# Revit family: Door-Slider-Fleetwood-3070-XXXX
name_source: partatom
category: Doors
revit_build: Autodesk Revit 2016 (Build: 20150714_1515(x64)
units: mm (PartAtom-declared; Revit-internal decimal feet)

## family parameters
Always vertical = Yes
Cut with Voids When Loaded = No
Host = Wall
OmniClass Number = 23.30.10.00
OmniClass Title = Doors
Room Calculation Point = No
Shared = No

## types (1)
- -
    1_Custom_Interlock_CL = 0 "
    2_Custom_Interlock_CL = 0 "
    3_Custom_Interlock_CL = 0 "
    Actuator_Height = 54 "
    Actuator_Vis = Placeholder
    Analytic Construction = <None>
    Archetype_Actuator = Hardware-Archetype_Actuator-Fleetwood
    Archetype_Flush_Pull_Vis = Placeholder
    Archetype_Flush_Pulls = No
    Archetype_Hardware = No
    Archetype_Narrow_Actuator = Hardware-Archetype_Narrow_Actuator-Fleetwood
    Archetype_Narrow_Actuator_Vis = Hardware-Archetype_Narrow_Actuator-Fleetwood
    Archetype_Narrow_Hardware = Yes
    Archetype_Narrow_Pull = Hardware-Archetype_Narrow_Pull-Fleetwood
    Archetype_Narrow_Pull_Vis = Hardware-Archetype_Narrow_Pull-Fleetwood
    Arrows = Yes
    Bottom_Rail = 5.15 "
    Configuration = XXXX
    Equal_Glass = Yes
    Exterior Wrap Overhang = 0.5 "
    Flush_Pull = Hardware-Archetype_Flush_Pull-Fleetwood
    Frame_&_Panel = Aluminum, Anodized Clear
    Function = Exterior
    Glazing = Glass
    Handle_Height = 45.75 "
    Hardware = Stainless Steel, Brushed
    Height = 96 "
    Interior Wrap Overhang = 0.5 "
    Interlock = 2.074 "
    Lead_Stile = 2.909 "
    Manufacturer = Fleetwood Windows and Doors
    Model = 3070
    Narrow_Pull_CL = 53.469 "
    P2_Location = 35.4128 "
    P3_Location = 69.9905 "
    Panel_Height = 94.4705 "
    Panel_Width_1 = 37.4868 "
    Panel_Width_2 = 36.6518 "
    Panel_Width_3 = 36.6518 "
    Panel_Width_4 = 37.4868 "
    Placeholder = Placeholder
    Rough Height = 96.25 "
    Rough Width = 144.5 "
    Shim_Space = 0.25 "
    Thickness = 7.632 "
    Top_Rail = 1.46 "
    Top_Rail_As_Bottom_Rail = No
    Type Image = <None>
    URL = www.fleetwoodusa.com
    Wall Closure = By host
    Width = 144 "

## geometry (parser evidence)
native form markers: Blend x4, Sweep x21
no freeform markers — native parametric forms only
